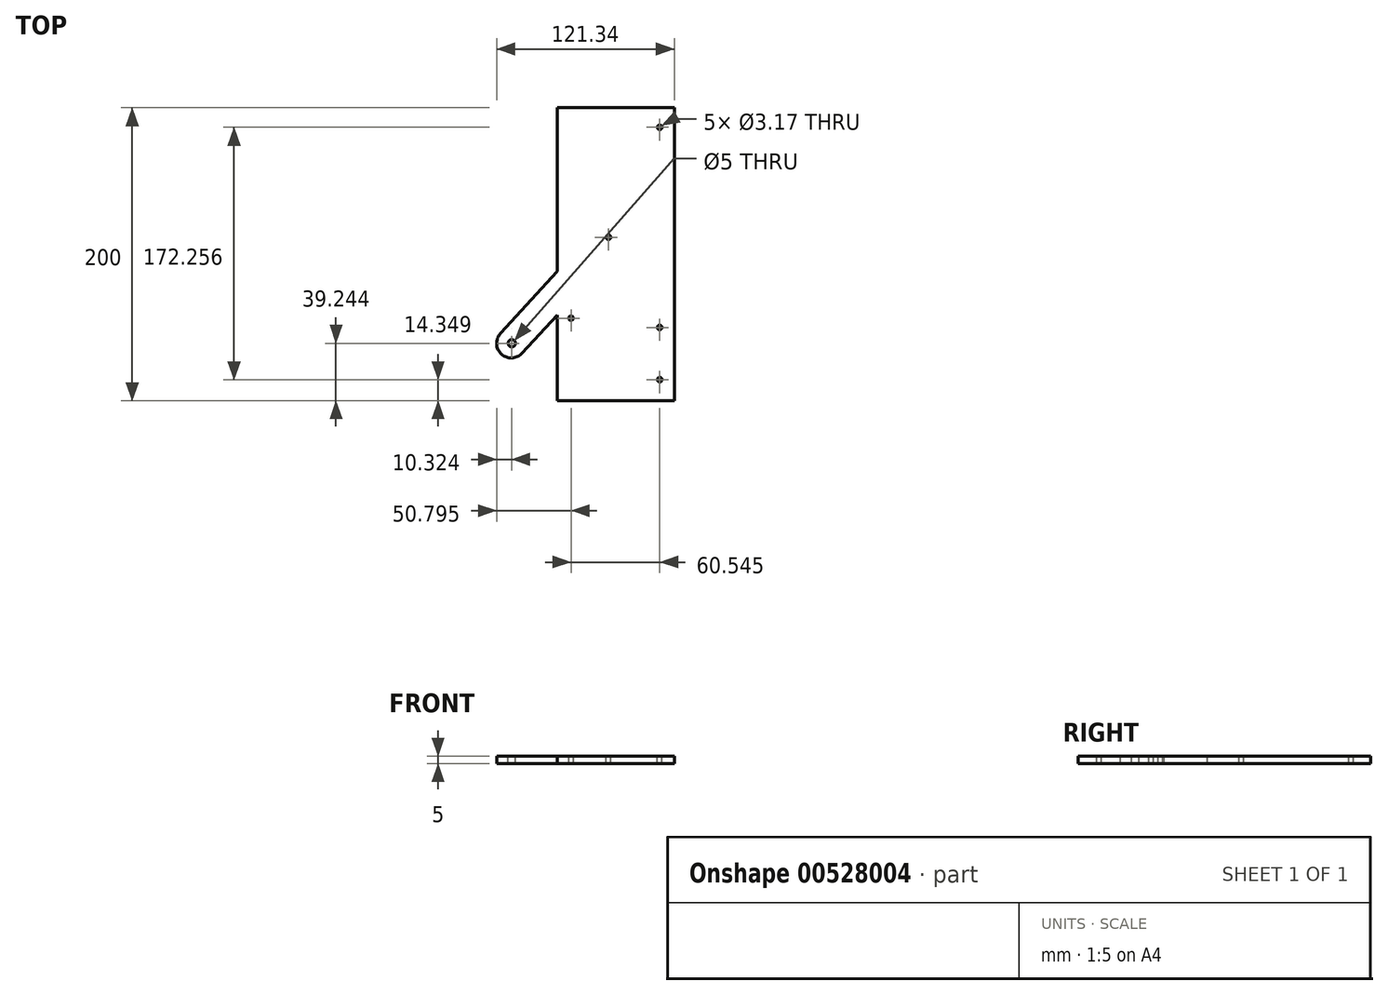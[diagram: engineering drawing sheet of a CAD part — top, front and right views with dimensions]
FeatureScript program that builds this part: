
annotation { "Feature Type Name" : "Feature", "Feature Type Description" : "" }
export const myFeature = defineFeature(function(context is Context, id is Id, definition is map)
    precondition{}
    {
        {
            var Q0;
            Q0=qCreatedBy(makeId("Top.planeOp"),FACE);
            var sketch = newSketch(context, id + "F0", { "sketchPlane" : qUnion([Q0])});
            skLineSegment(sketch, "E0.bottom", {"start": v(100, 150) * mm, "end": v(-100, 150) * mm});
            skLineSegment(sketch, "E0.top", {"start": v(100, -150) * mm, "end": v(-100, -150) * mm});
            skLineSegment(sketch, "E0.left", {"start": v(100, 150) * mm, "end": v(100, -150) * mm});
            skLineSegment(sketch, "E0.right", {"start": v(-100, 150) * mm, "end": v(-100, -150) * mm});
            skPoint(sketch, "E0.middle", {"position": v(0, 0) * mm});
            skSolve(sketch);
        }
        {
            var Q0;
            Q0=qSketchRegion(id+"F0",true);
            extrude(context, id + "F1", {"entities" : qUnion([Q0]), "depth" : 5 * mm});
        }
        {
            var Q0;
            Q0=makeQuery(id+"F1.opExtrude","CAP_FACE",FACE,{"disambiguationData":[OSD([sQuery(id+"F0.wireOp",EDGE,"E0.bottom"),sQuery(id+"F0.wireOp",EDGE,"E0.top"),sQuery(id+"F0.wireOp",EDGE,"E0.left"),sQuery(id+"F0.wireOp",EDGE,"E0.right")])],"isStart":false});
            var sketch = newSketch(context, id + "F2", { "sketchPlane" : qUnion([Q0])});
            skCircle(sketch, "E1", {"center": v(0, 0) * mm, "radius": 1.59 * mm});
            skCircle(sketch, "E2", {"center": v(0, -35.65) * mm, "radius": 1.59 * mm});
            skCircle(sketch, "E3", {"center": v(-60.54, 6.35) * mm, "radius": 1.59 * mm});
            skCircle(sketch, "E4", {"center": v(-35, 61.6) * mm, "radius": 1.59 * mm});
            skCircle(sketch, "E5", {"center": v(0, 136.6) * mm, "radius": 1.59 * mm});
            skLineSegment(sketch, "E6", {"start": v(0, 0) * mm, "end": v(-73.74, 0) * mm, "construction": true});
            skSolve(sketch);
        }
        {
            var Q0;
            Q0=qSketchRegion(id+"F2",true);
            extrude(context, id + "F3", {"entities" : qUnion([Q0]), "operationType" : NewBodyOperationType.REMOVE, "endBound" : BoundingType.THROUGH_ALL, "oppositeDirection" : true, "depth" : 25 * mm});
        }
        {
            var Q0;
            Q0=makeQuery(id+"F1.opExtrude","CAP_FACE",FACE,{"disambiguationData":[OSD([sQuery(id+"F0.wireOp",EDGE,"E0.bottom"),sQuery(id+"F0.wireOp",EDGE,"E0.top"),sQuery(id+"F0.wireOp",EDGE,"E0.left"),sQuery(id+"F0.wireOp",EDGE,"E0.right")])],"isStart":false});
            var sketch = newSketch(context, id + "F4", { "sketchPlane" : qUnion([Q0])});
            skLineSegment(sketch, "E7.bottom", {"start": v(-70, 150) * mm, "end": v(10, 150) * mm});
            skLineSegment(sketch, "E7.top", {"start": v(-70, -50) * mm, "end": v(10, -50) * mm});
            skLineSegment(sketch, "E7.left", {"start": v(-70, 150) * mm, "end": v(-70, -50) * mm});
            skLineSegment(sketch, "E7.right", {"start": v(10, 150) * mm, "end": v(10, -50) * mm});
            skLineSegment(sketch, "E8.bottom", {"start": v(-100, 150) * mm, "end": v(100, 150) * mm});
            skLineSegment(sketch, "E8.top", {"start": v(-100, -150) * mm, "end": v(100, -150) * mm});
            skLineSegment(sketch, "E8.left", {"start": v(-100, 150) * mm, "end": v(-100, -150) * mm});
            skLineSegment(sketch, "E8.right", {"start": v(100, 150) * mm, "end": v(100, -150) * mm});
            skSolve(sketch);
        }
        {
            var Q0;
            Q0=makeQuery(id+"F4.imprint","IMPRINT",FACE,{"disambiguationData":[TD([[makeQuery(id+"F4.imprint","IMPRINT",EDGE,{"derivedFrom":sQuery(id+"F4.wireOp",EDGE,"E7.top")}),-1.0]])]});
            var Q1;
            Q1=makeQuery(id+"F4.imprint","IMPRINT",FACE,{"disambiguationData":[TD([[makeQuery(id+"F4.imprint","IMPRINT",EDGE,{"derivedFrom":makeQuery(id+"F3.boolean.opBoolean","COPY",EDGE,{"derivedFrom":makeQuery(id+"F3.opExtrude","CAP_EDGE",EDGE,{"disambiguationData":[OSD([sQuery(id+"F2.wireOp",EDGE,"E1")])],"isStart":true})})}),1.0]])]});
            var Q2;
            Q2=makeQuery(id+"F4.imprint","IMPRINT",FACE,{"disambiguationData":[TD([[makeQuery(id+"F4.imprint","IMPRINT",EDGE,{"derivedFrom":makeQuery(id+"F3.boolean.opBoolean","COPY",EDGE,{"derivedFrom":makeQuery(id+"F3.opExtrude","CAP_EDGE",EDGE,{"disambiguationData":[OSD([sQuery(id+"F2.wireOp",EDGE,"E2")])],"isStart":true})})}),1.0]])]});
            var Q3;
            Q3=makeQuery(id+"F4.imprint","IMPRINT",FACE,{"disambiguationData":[TD([[makeQuery(id+"F4.imprint","IMPRINT",EDGE,{"derivedFrom":makeQuery(id+"F3.boolean.opBoolean","COPY",EDGE,{"derivedFrom":makeQuery(id+"F3.opExtrude","CAP_EDGE",EDGE,{"disambiguationData":[OSD([sQuery(id+"F2.wireOp",EDGE,"E3")])],"isStart":true})})}),1.0]])]});
            var Q4;
            Q4=makeQuery(id+"F4.imprint","IMPRINT",FACE,{"disambiguationData":[TD([[makeQuery(id+"F4.imprint","IMPRINT",EDGE,{"derivedFrom":makeQuery(id+"F3.boolean.opBoolean","COPY",EDGE,{"derivedFrom":makeQuery(id+"F3.opExtrude","CAP_EDGE",EDGE,{"disambiguationData":[OSD([sQuery(id+"F2.wireOp",EDGE,"E4")])],"isStart":true})})}),1.0]])]});
            var Q5;
            Q5=makeQuery(id+"F4.imprint","IMPRINT",FACE,{"disambiguationData":[TD([[makeQuery(id+"F4.imprint","IMPRINT",EDGE,{"derivedFrom":makeQuery(id+"F3.boolean.opBoolean","COPY",EDGE,{"derivedFrom":makeQuery(id+"F3.opExtrude","CAP_EDGE",EDGE,{"disambiguationData":[OSD([sQuery(id+"F2.wireOp",EDGE,"E5")])],"isStart":true})})}),1.0]])]});
            extrude(context, id + "F5", {"entities" : qUnion([Q0, Q1, Q2, Q3, Q4, Q5]), "operationType" : NewBodyOperationType.REMOVE, "oppositeDirection" : true, "depth" : 25 * mm});
        }
        {
            var Q0;
            Q0=makeQuery(id+"F1.opExtrude","CAP_FACE",FACE,{"disambiguationData":[OSD([sQuery(id+"F0.wireOp",EDGE,"E0.bottom"),sQuery(id+"F0.wireOp",EDGE,"E0.top"),sQuery(id+"F0.wireOp",EDGE,"E0.left"),sQuery(id+"F0.wireOp",EDGE,"E0.right")])],"isStart":false});
            var sketch = newSketch(context, id + "F6", { "sketchPlane" : qUnion([Q0])});
            skLineSegment(sketch, "E9", {"start": v(-35, 61.6) * mm, "end": v(-35, -119.65) * mm});
            skLineSegment(sketch, "E10", {"start": v(-35, -119.65) * mm, "end": v(-35, 61.6) * mm});
            skLineSegment(sketch, "E11", {"start": v(0, 135.02) * mm, "end": v(0, 0) * mm});
            skLineSegment(sketch, "E12", {"start": v(-35, 61.6) * mm, "end": v(0, 99.8) * mm});
            skLineSegment(sketch, "E13", {"start": v(-35, 61.6) * mm, "end": v(-60.54, 6.35) * mm});
            skLineSegment(sketch, "E14", {"start": v(0, 99.8) * mm, "end": v(-101.34, -10.8) * mm});
            skArc(sketch, "E15.0.startCap", {"start": v(-7.37, 106.56) * mm, "mid": v(6.76, 107.17) * mm, "end": v(7.37, 93.05) * mm});
            skArc(sketch, "E15.0.endCap", {"start": v(-93.97, -17.55) * mm, "mid": v(-108.1, -18.16) * mm, "end": v(-108.71, -4.03) * mm});
            skLineSegment(sketch, "E15.0.left", {"start": v(7.37, 93.05) * mm, "end": v(-93.97, -17.55) * mm});
            skLineSegment(sketch, "E15.0.right", {"start": v(-7.37, 106.56) * mm, "end": v(-108.71, -4.03) * mm});
            skCircle(sketch, "E16", {"center": v(-35, 61.6) * mm, "radius": 1.59 * mm});
            skSolve(sketch);
        }
        {
            var Q0;
            Q0=qSketchRegion(id+"F6",true);
            extrude(context, id + "F7", {"entities" : qUnion([Q0]), "operationType" : NewBodyOperationType.ADD, "oppositeDirection" : true, "depth" : 5 * mm});
        }
        {
            var Q0;
            Q0=makeQuery(id+"F7.boolean.opBoolean","MERGE",FACE,{"derivedFrom":[makeQuery(id+"F1.opExtrude","CAP_FACE",FACE,{"disambiguationData":[OSD([sQuery(id+"F0.wireOp",EDGE,"E0.bottom"),sQuery(id+"F0.wireOp",EDGE,"E0.top"),sQuery(id+"F0.wireOp",EDGE,"E0.left"),sQuery(id+"F0.wireOp",EDGE,"E0.right")])],"isStart":false}),makeQuery(id+"F7.opExtrude","CAP_FACE",FACE,{"disambiguationData":[OSD([sQuery(id+"F6.wireOp",EDGE,"E15.0.startCap"),sQuery(id+"F6.wireOp",EDGE,"E15.0.endCap"),sQuery(id+"F6.wireOp",EDGE,"E15.0.left"),sQuery(id+"F6.wireOp",EDGE,"E15.0.right"),sQuery(id+"F6.wireOp",EDGE,"E16")])],"isStart":true})]});
            var sketch = newSketch(context, id + "F8", { "sketchPlane" : qUnion([Q0])});
            skCircle(sketch, "E17", {"center": v(-101.02, -10.76) * mm, "radius": 2.5 * mm});
            skCircle(sketch, "E18", {"center": v(-101.34, -10.8) * mm, "radius": 10 * mm});
            skPoint(sketch, "E18.first.point", {"position": v(-108.71, -4.03) * mm});
            skPoint(sketch, "E18.second.point", {"position": v(-93.97, -17.55) * mm});
            skPoint(sketch, "E18.third.point.positionSnap0", {"position": v(-108.1, -18.16) * mm});
            skSolve(sketch);
        }
        {
            var Q0;
            Q0=makeQuery(id+"F8.imprint","IMPRINT",FACE,{"disambiguationData":[TD([[makeQuery(id+"F8.imprint","IMPRINT",EDGE,{"derivedFrom":sQuery(id+"F8.wireOp",EDGE,"E17")}),1.0]])]});
            extrude(context, id + "F9", {"entities" : qUnion([Q0]), "operationType" : NewBodyOperationType.REMOVE, "oppositeDirection" : true, "depth" : 25 * mm});
        }
    });
